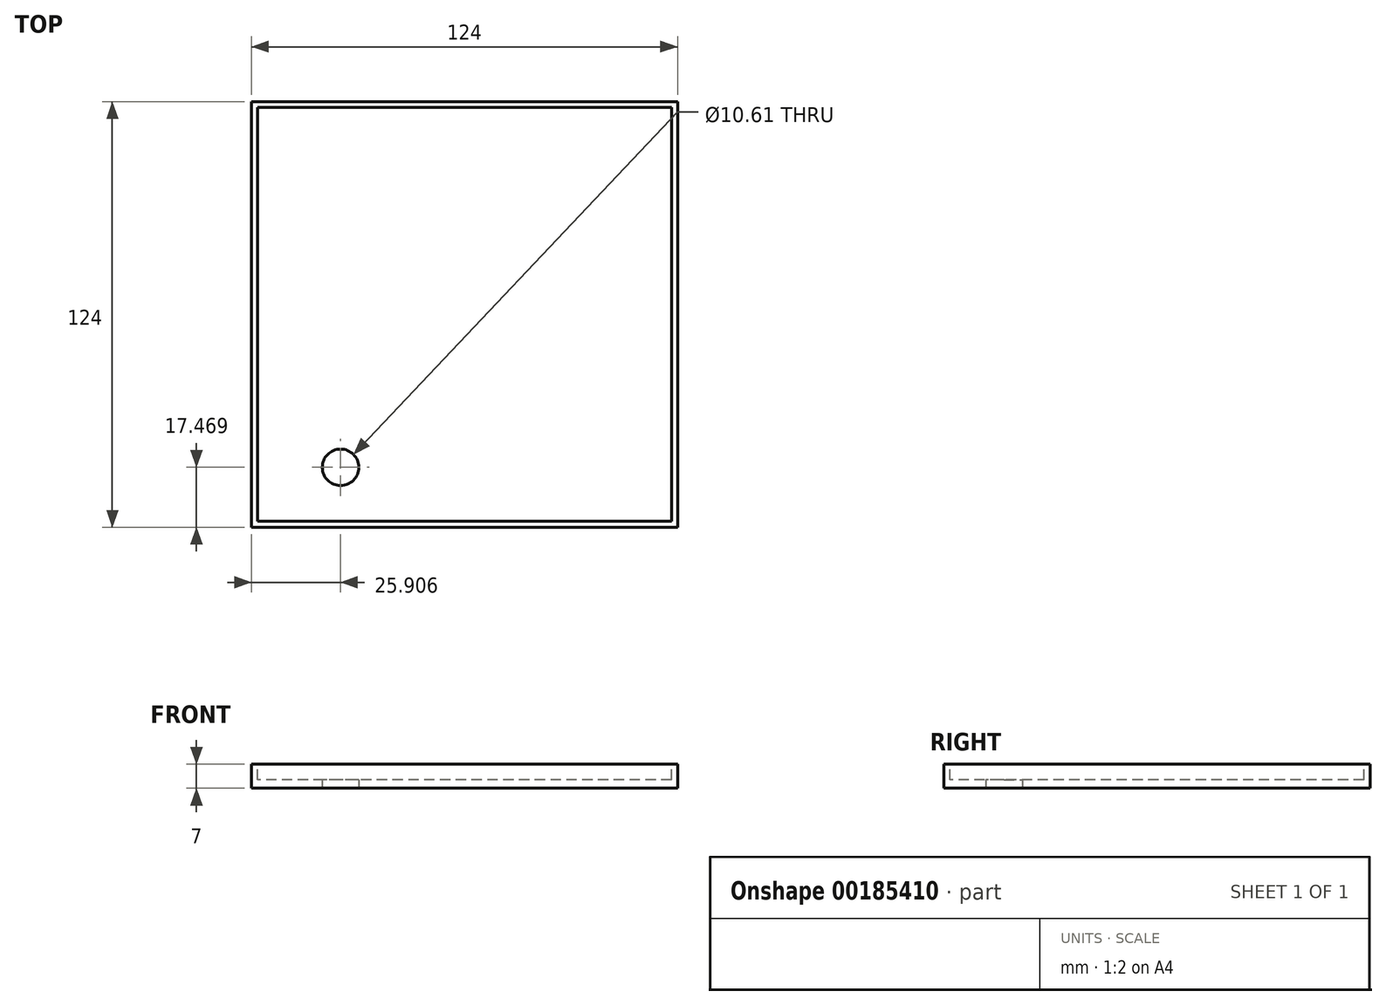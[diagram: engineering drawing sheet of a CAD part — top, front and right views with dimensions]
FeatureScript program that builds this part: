
annotation { "Feature Type Name" : "Feature", "Feature Type Description" : "" }
export const myFeature = defineFeature(function(context is Context, id is Id, definition is map)
    precondition{}
    {
        {
            var Q0;
            Q0=qCreatedBy(makeId("Top.planeOp"),FACE);
            var sketch = newSketch(context, id + "F0", { "sketchPlane" : qUnion([Q0])});
            skLineSegment(sketch, "E0.bottom", {"start": v(-62, 62) * mm, "end": v(62, 62) * mm});
            skLineSegment(sketch, "E0.top", {"start": v(-62, -62) * mm, "end": v(62, -62) * mm});
            skLineSegment(sketch, "E0.left", {"start": v(-62, 62) * mm, "end": v(-62, -62) * mm});
            skLineSegment(sketch, "E0.right", {"start": v(62, 62) * mm, "end": v(62, -62) * mm});
            skPoint(sketch, "E0.middle", {"position": v(0, 0) * mm});
            skSolve(sketch);
        }
        {
            var Q0;
            Q0=makeQuery(id+"F0.imprint","IMPRINT",FACE,{"disambiguationData":[TD([[makeQuery(id+"F0.imprint","IMPRINT",EDGE,{"derivedFrom":sQuery(id+"F0.wireOp",EDGE,"E0.bottom")}),-1.0]])]});
            extrude(context, id + "F1", {"entities" : qUnion([Q0]), "depth" : 7 * mm});
        }
        {
            var Q0;
            Q0=makeQuery(id+"F1.opExtrude","CAP_FACE",FACE,{"disambiguationData":[OSD([sQuery(id+"F0.wireOp",EDGE,"E0.bottom"),sQuery(id+"F0.wireOp",EDGE,"E0.top"),sQuery(id+"F0.wireOp",EDGE,"E0.left"),sQuery(id+"F0.wireOp",EDGE,"E0.right")])],"isStart":false});
            var sketch = newSketch(context, id + "F2", { "sketchPlane" : qUnion([Q0])});
            skLineSegment(sketch, "E1.bottom", {"start": v(60.25, 60.25) * mm, "end": v(-60.25, 60.25) * mm});
            skLineSegment(sketch, "E1.top", {"start": v(60.25, -60.25) * mm, "end": v(-60.25, -60.25) * mm});
            skLineSegment(sketch, "E1.left", {"start": v(60.25, 60.25) * mm, "end": v(60.25, -60.25) * mm});
            skLineSegment(sketch, "E1.right", {"start": v(-60.25, 60.25) * mm, "end": v(-60.25, -60.25) * mm});
            skPoint(sketch, "E1.middle", {"position": v(0, 0) * mm});
            skSolve(sketch);
        }
        {
            var Q0;
            Q0=makeQuery(id+"F2.imprint","IMPRINT",FACE,{"disambiguationData":[TD([[makeQuery(id+"F2.imprint","IMPRINT",EDGE,{"derivedFrom":sQuery(id+"F2.wireOp",EDGE,"E1.bottom")}),1.0]])]});
            extrude(context, id + "F3", {"entities" : qUnion([Q0]), "operationType" : NewBodyOperationType.REMOVE, "oppositeDirection" : true, "depth" : 4.5 * mm});
        }
        {
            var Q0;
            Q0=makeQuery(id+"F1.opExtrude","CAP_FACE",FACE,{"disambiguationData":[OSD([sQuery(id+"F0.wireOp",EDGE,"E0.bottom"),sQuery(id+"F0.wireOp",EDGE,"E0.top"),sQuery(id+"F0.wireOp",EDGE,"E0.left"),sQuery(id+"F0.wireOp",EDGE,"E0.right")])],"isStart":true});
            var sketch = newSketch(context, id + "F4", { "sketchPlane" : qUnion([Q0])});
            skCircle(sketch, "E2", {"center": v(-36.1, 44.53) * mm, "radius": 5.3 * mm});
            skSolve(sketch);
        }
        {
            var Q0;
            Q0 = qSketchRegion(id + "F4", true);
            extrude(context, id + "F5", {"entities" : qUnion([Q0]), "operationType" : NewBodyOperationType.REMOVE, "endBound" : BoundingType.THROUGH_ALL, "oppositeDirection" : true, "depth" : 25 * mm});
        }
    });
